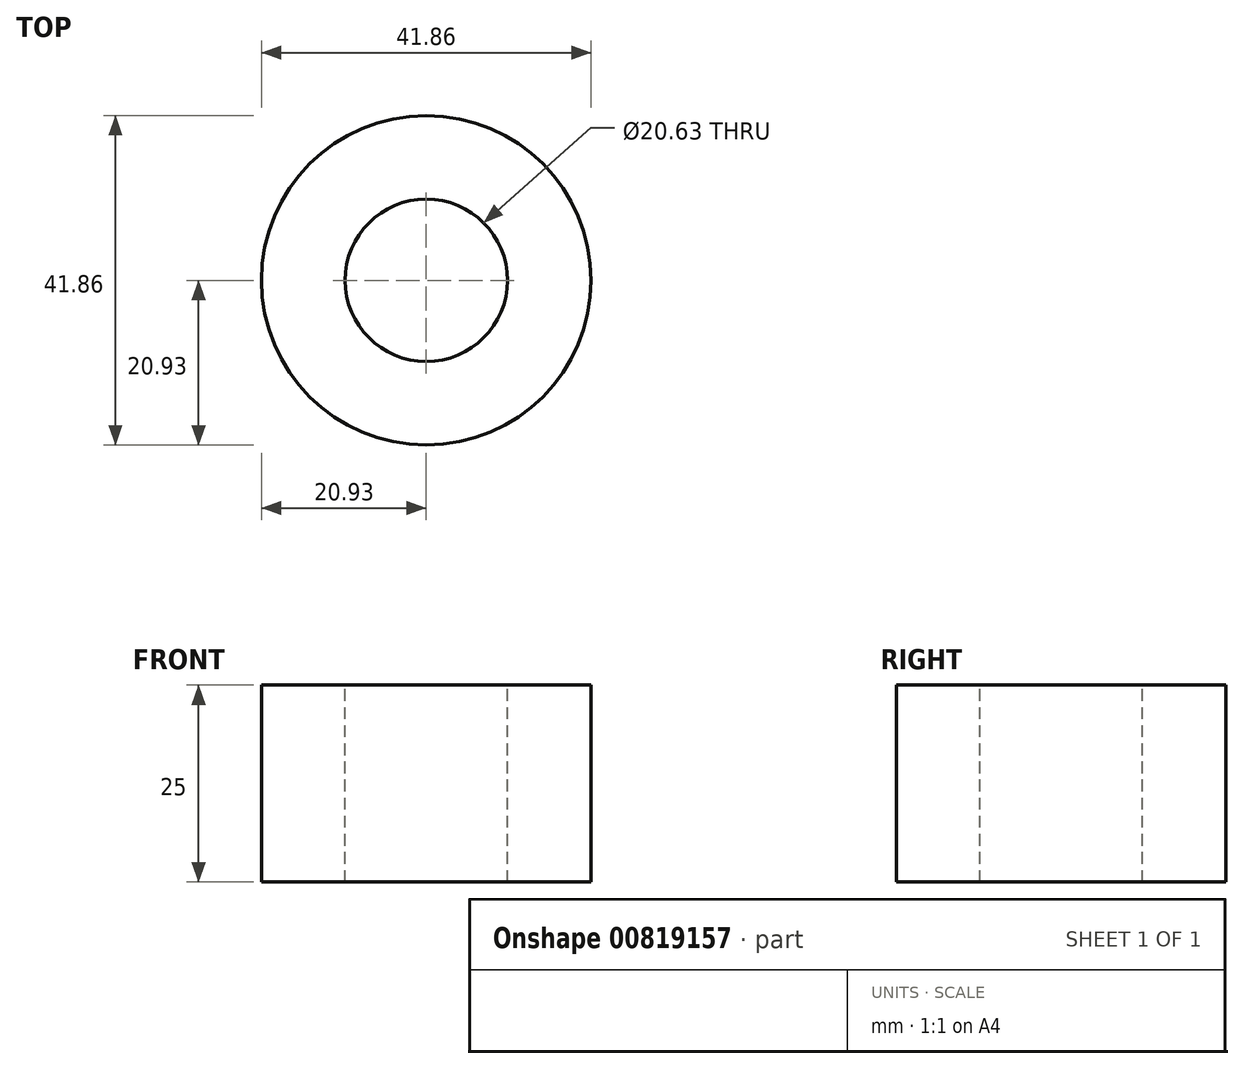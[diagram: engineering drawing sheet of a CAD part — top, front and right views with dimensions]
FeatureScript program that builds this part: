
annotation { "Feature Type Name" : "Feature", "Feature Type Description" : "" }
export const myFeature = defineFeature(function(context is Context, id is Id, definition is map)
    precondition{}
    {
        {
            var Q0;
            Q0=qCreatedBy(makeId("Top.planeOp"),FACE);
            var sketch = newSketch(context, id + "F0", { "sketchPlane" : qUnion([Q0])});
            skCircle(sketch, "E0", {"center": v(0, 0) * mm, "radius": 20.93 * mm});
            skSolve(sketch);
        }
        {
            var Q0;
            Q0=makeQuery(id+"F0.imprint","IMPRINT",FACE,{"disambiguationData":[TD([[makeQuery(id+"F0.imprint","IMPRINT",EDGE,{"derivedFrom":sQuery(id+"F0.wireOp",EDGE,"E0")}),1.0]])]});
            extrude(context, id + "F1", {"entities" : qUnion([Q0]), "depth" : 25 * mm, "offsetDistance" : 25 * mm});
        }
        {
            var Q0;
            Q0=makeQuery(id+"F1.opExtrude","CAP_FACE",FACE,{"disambiguationData":[OSD([sQuery(id+"F0.wireOp",EDGE,"E0")])],"isStart":false});
            var sketch = newSketch(context, id + "F2", { "sketchPlane" : qUnion([Q0])});
            skCircle(sketch, "E1", {"center": v(0, 0) * mm, "radius": 9.21 * mm});
            skSolve(sketch);
        }
        {
            var Q0;
            Q0=makeQuery(id+"F2.imprint","IMPRINT",FACE,{"disambiguationData":[TD([[makeQuery(id+"F2.imprint","IMPRINT",EDGE,{"derivedFrom":sQuery(id+"F2.wireOp",EDGE,"E1")}),1.0]])]});
            extrude(context, id + "F3", {"entities" : qUnion([Q0]), "operationType" : NewBodyOperationType.ADD, "oppositeDirection" : true, "depth" : 25 * mm, "offsetDistance" : 25 * mm});
        }
        {
            var Q0;
            Q0=makeQuery(id+"F1.opExtrude","CAP_FACE",FACE,{"disambiguationData":[OSD([sQuery(id+"F0.wireOp",EDGE,"E0")])],"isStart":false});
            var sketch = newSketch(context, id + "F4", { "sketchPlane" : qUnion([Q0])});
            skCircle(sketch, "E2", {"center": v(0, 0) * mm, "radius": 10.32 * mm});
            skSolve(sketch);
        }
        {
            var Q0;
            Q0 = qSketchRegion(id + "F4", true);
            extrude(context, id + "F5", {"entities" : qUnion([Q0]), "operationType" : NewBodyOperationType.REMOVE, "oppositeDirection" : true, "depth" : 25 * mm, "offsetDistance" : 25 * mm});
        }
    });
